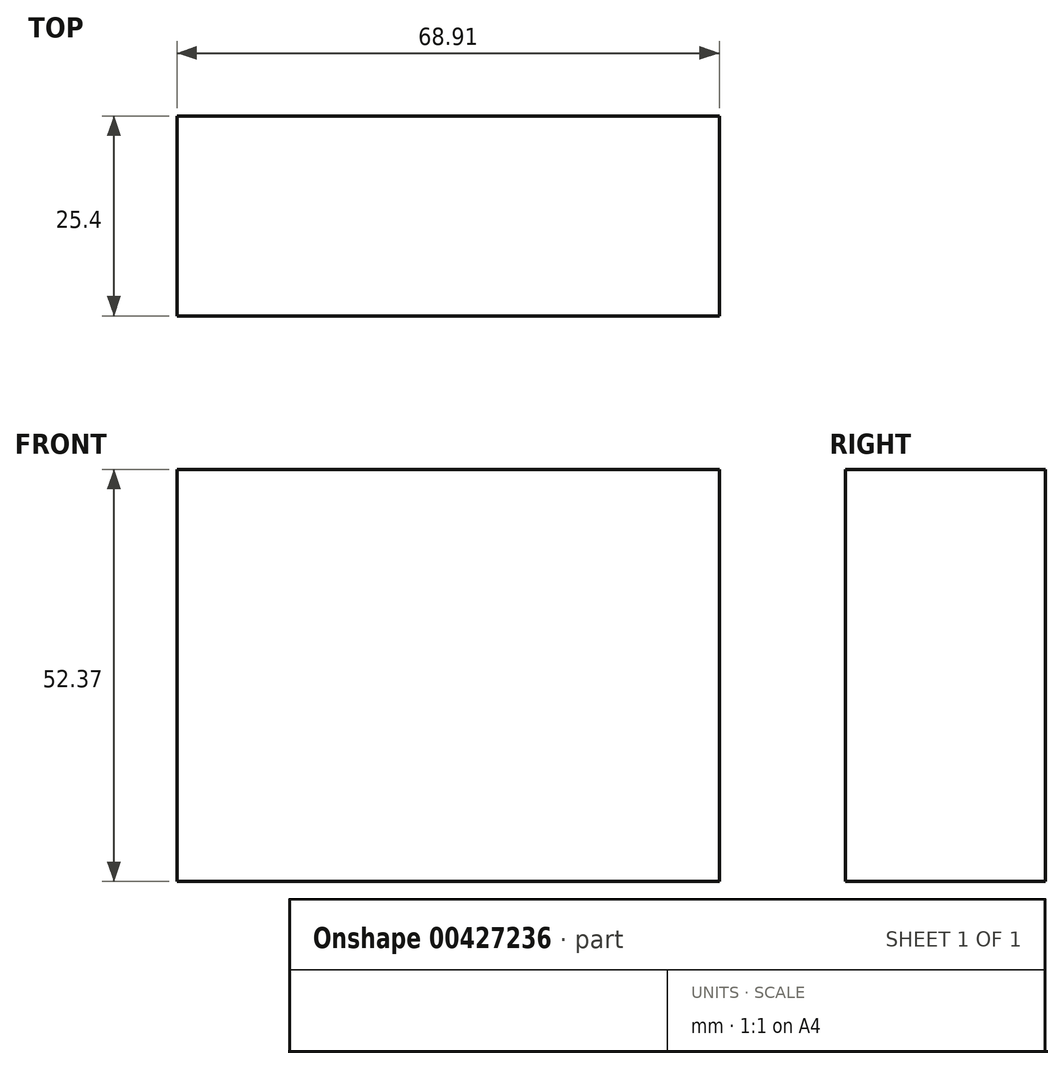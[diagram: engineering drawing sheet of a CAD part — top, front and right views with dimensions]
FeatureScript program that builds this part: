
annotation { "Feature Type Name" : "Feature", "Feature Type Description" : "" }
export const myFeature = defineFeature(function(context is Context, id is Id, definition is map)
    precondition{}
    {
        {
            var Q0;
            Q0=qCreatedBy(makeId("Front.planeOp"),FACE);
            var sketch = newSketch(context, id + "F0", { "sketchPlane" : qUnion([Q0])});
            skLineSegment(sketch, "E0.bottom", {"start": v(0, 0) * mm, "end": v(68.91, 0) * mm});
            skLineSegment(sketch, "E0.top", {"start": v(0, 52.37) * mm, "end": v(68.91, 52.37) * mm});
            skLineSegment(sketch, "E0.left", {"start": v(0, 0) * mm, "end": v(0, 52.37) * mm});
            skLineSegment(sketch, "E0.right", {"start": v(68.91, 0) * mm, "end": v(68.91, 52.37) * mm});
            skSolve(sketch);
        }
        {
            var Q0;
            Q0 = qSketchRegion(id + "F0", true);
            extrude(context, id + "F1", {"entities" : qUnion([Q0]), "oppositeDirection" : true, "depth" : 25.4 * mm});
        }
    });
